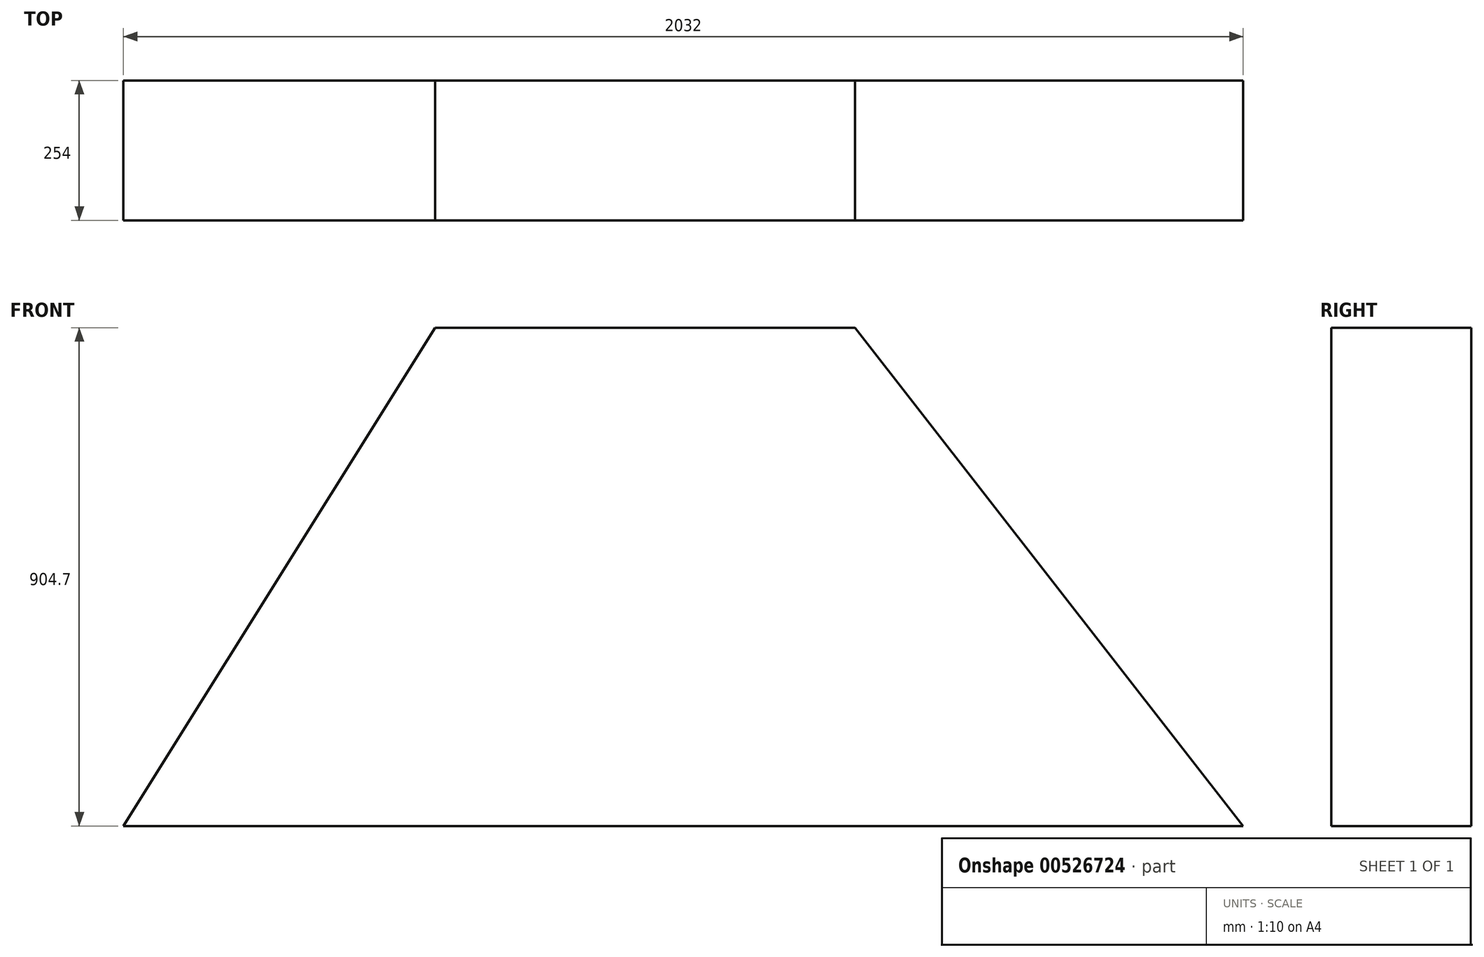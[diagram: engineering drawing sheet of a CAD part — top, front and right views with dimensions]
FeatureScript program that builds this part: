
annotation { "Feature Type Name" : "Feature", "Feature Type Description" : "" }
export const myFeature = defineFeature(function(context is Context, id is Id, definition is map)
    precondition{}
    {
        {
            var Q0;
            Q0=qCreatedBy(makeId("Front.planeOp"),FACE);
            var sketch = newSketch(context, id + "F0", { "sketchPlane" : qUnion([Q0])});
            skLineSegment(sketch, "E0", {"start": v(0, 0) * mm, "end": v(2032, 0) * mm});
            skLineSegment(sketch, "E1", {"start": v(0, 0) * mm, "end": v(565.32, 904.7) * mm});
            skLineSegment(sketch, "E2", {"start": v(565.32, 904.7) * mm, "end": v(1327.32, 904.7) * mm});
            skLineSegment(sketch, "E3", {"start": v(1327.32, 904.7) * mm, "end": v(2032, 0) * mm});
            skSolve(sketch);
        }
        {
            var Q0;
            Q0=makeQuery(id+"F0.imprint","IMPRINT",FACE,{"disambiguationData":[TD([[makeQuery(id+"F0.imprint","IMPRINT",EDGE,{"derivedFrom":sQuery(id+"F0.wireOp",EDGE,"E0")}),1.0]])]});
            extrude(context, id + "F1", {"entities" : qUnion([Q0]), "depth" : 254 * mm, "offsetDistance" : 25.4 * mm});
        }
    });
